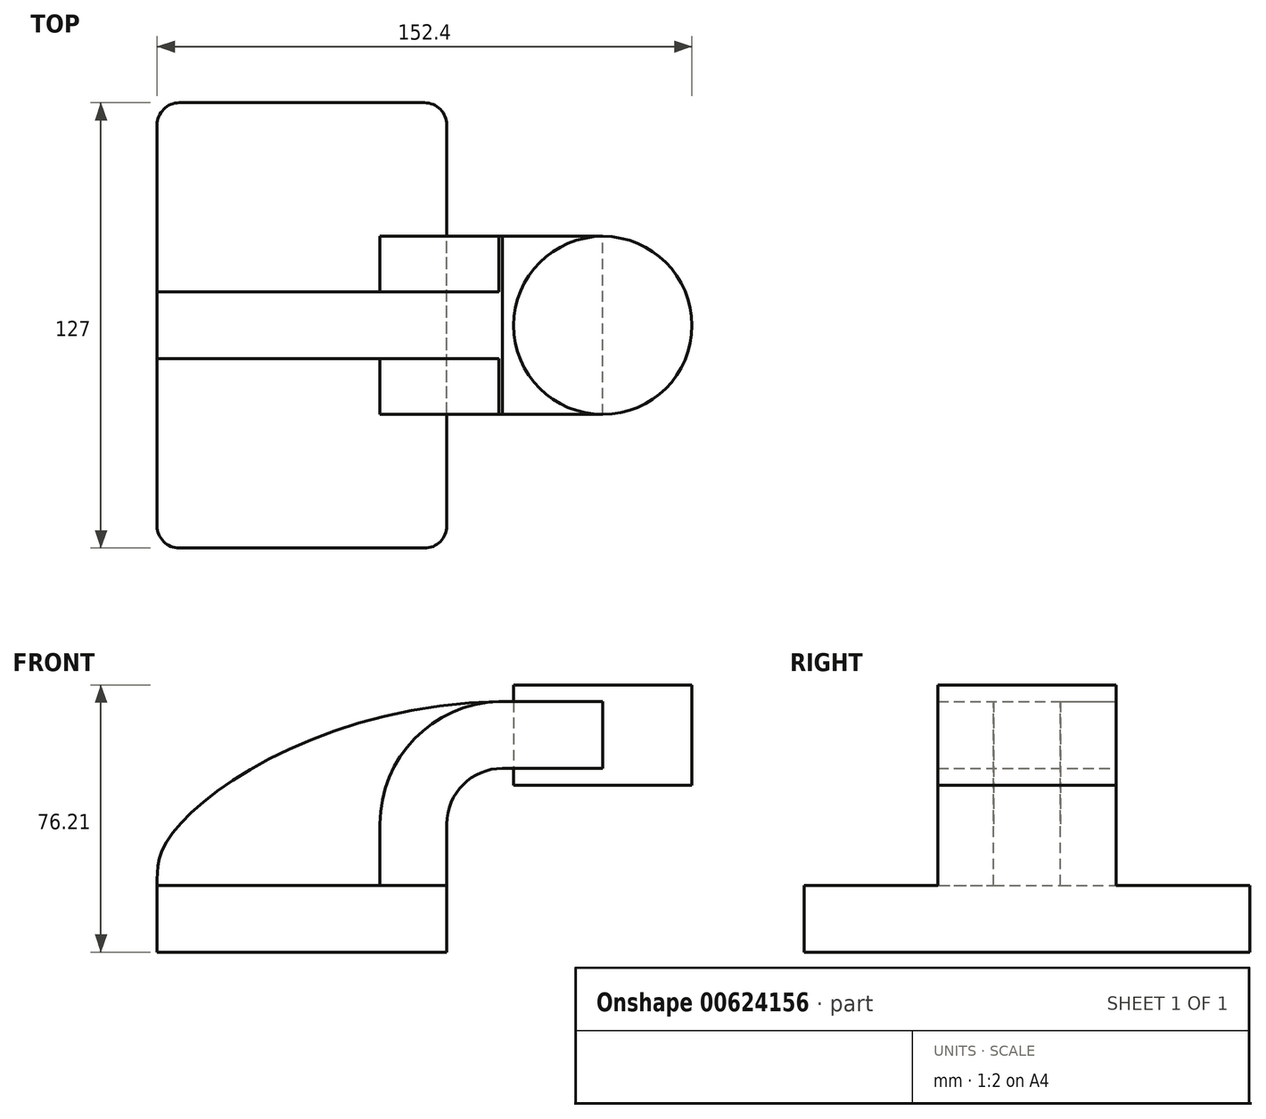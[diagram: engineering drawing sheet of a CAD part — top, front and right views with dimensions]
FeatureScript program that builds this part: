
annotation { "Feature Type Name" : "Feature", "Feature Type Description" : "" }
export const myFeature = defineFeature(function(context is Context, id is Id, definition is map)
    precondition{}
    {
        {
            var Q0;
            Q0=qCreatedBy(makeId("Front.planeOp"),FACE);
            var sketch = newSketch(context, id + "F0", { "sketchPlane" : qUnion([Q0])});
            skLineSegment(sketch, "E0.bottom", {"start": v(41.8, 9.52) * mm, "end": v(-40.75, 9.53) * mm});
            skLineSegment(sketch, "E0.top", {"start": v(41.8, -9.53) * mm, "end": v(-40.75, -9.52) * mm});
            skLineSegment(sketch, "E0.left", {"start": v(41.8, 9.52) * mm, "end": v(41.8, -9.53) * mm});
            skLineSegment(sketch, "E0.right", {"start": v(-40.75, 9.53) * mm, "end": v(-40.75, -9.52) * mm});
            skPoint(sketch, "E0.middle", {"position": v(0.53, 0) * mm});
            skLineSegment(sketch, "E1.bottom", {"start": v(60.85, 66.67) * mm, "end": v(111.65, 66.67) * mm});
            skLineSegment(sketch, "E1.top", {"start": v(60.85, 38.1) * mm, "end": v(111.65, 38.1) * mm});
            skLineSegment(sketch, "E1.left", {"start": v(60.85, 66.67) * mm, "end": v(60.85, 38.1) * mm});
            skLineSegment(sketch, "E1.right", {"start": v(111.65, 66.67) * mm, "end": v(111.65, 38.1) * mm});
            skPoint(sketch, "E1.middle", {"position": v(86.25, 52.39) * mm});
            skPoint(sketch, "E2.endSnap0", {"position": v(60.85, 52.39) * mm});
            skLineSegment(sketch, "E3", {"start": v(41.8, 9.52) * mm, "end": v(41.8, 27) * mm});
            skArc(sketch, "E4", {"start": v(41.8, 27) * mm, "mid": v(46.45, 38.23) * mm, "end": v(57.68, 42.88) * mm});
            skLineSegment(sketch, "E5", {"start": v(57.68, 42.88) * mm, "end": v(86.25, 42.88) * mm});
            skLineSegment(sketch, "E6.0", {"start": v(57.68, 61.93) * mm, "end": v(86.25, 61.93) * mm});
            skArc(sketch, "E6.1", {"start": v(22.75, 27) * mm, "mid": v(32.98, 51.7) * mm, "end": v(57.68, 61.93) * mm});
            skLineSegment(sketch, "E6.2", {"start": v(22.75, 9.52) * mm, "end": v(22.75, 27) * mm});
            skLineSegment(sketch, "E7", {"start": v(86.25, 38.1) * mm, "end": v(86.25, 66.67) * mm});
            skFitSpline(sketch, "E8", {"points": [v(-40.75, 9.52) * mm, v(-38.27, 21.6) * mm, v(57.68, 61.93) * mm], "startDerivative": vector(1.49, 38.85) * mm, "endDerivative": vector(202.41, 2.3) * mm});
            skSolve(sketch);
        }
        {
            var Q0;
            Q0=makeQuery(id+"F0.imprint","IMPRINT",FACE,{"disambiguationData":[TD([[makeQuery(id+"F0.imprint","IMPRINT",EDGE,{"derivedFrom":sQuery(id+"F0.wireOp",EDGE,"E0.top")}),-1.0]])]});
            extrude(context, id + "F1", {"entities" : qUnion([Q0]), "endBound" : BoundingType.SYMMETRIC, "depth" : 127 * mm, "offsetDistance" : 25.4 * mm});
        }
        {
            var Q0;
            {var subQ1=sQuery(id+"F0.wireOp",EDGE,"E3");Q0=makeQuery(id+"F0.imprint","IMPRINT",FACE,{"disambiguationData":[TD([[makeQuery(id+"F0.imprint","IMPRINT",EDGE,{"derivedFrom":subQ1}),1.0]])]});}
            var Q1;
            {var subQ0=sQuery(id+"F0.wireOp",EDGE,"E6.0");var subQ1=sQuery(id+"F0.wireOp",EDGE,"E1.left");var subQ2=makeQuery(id+"F0.imprint","INTERSECT",VERTEX,{"derivedFrom":[subQ1,subQ0]});Q1=makeQuery(id+"F0.imprint","IMPRINT",FACE,{"disambiguationData":[TD([[makeQuery(id+"F0.imprint","IMPRINT",EDGE,{"disambiguationData":[TD([[subQ2,-1.0]])],"derivedFrom":subQ1}),1.0]])]});}
            extrude(context, id + "F2", {"entities" : qUnion([Q0, Q1]), "operationType" : NewBodyOperationType.ADD, "endBound" : BoundingType.SYMMETRIC, "depth" : 50.8 * mm, "offsetDistance" : 25.4 * mm});
        }
        {
            var Q0;
            {var subQ3=sQuery(id+"F0.wireOp",EDGE,"E6.2");Q0=makeQuery(id+"F0.imprint","IMPRINT",FACE,{"disambiguationData":[TD([[makeQuery(id+"F0.imprint","IMPRINT",EDGE,{"derivedFrom":subQ3}),1.0]])]});}
            extrude(context, id + "F3", {"entities" : qUnion([Q0]), "operationType" : NewBodyOperationType.ADD, "endBound" : BoundingType.SYMMETRIC, "depth" : 19.05 * mm, "offsetDistance" : 25.4 * mm});
        }
        {
            var Q0;
            {var subQ4=sQuery(id+"F0.wireOp",EDGE,"E1.right");Q0=makeQuery(id+"F0.imprint","IMPRINT",FACE,{"disambiguationData":[TD([[makeQuery(id+"F0.imprint","IMPRINT",EDGE,{"derivedFrom":subQ4}),-1.0]])]});}
            var Q1;
            Q1=sQuery(id+"F0.wireOp",EDGE,"E7");
            revolve(context, id + "F4", {"entities" : qUnion([Q0]), "axis" : qUnion([Q1]), "revolveType" : RevolveType.FULL});
        }
        {
            var Q0;
            Q0=makeQuery(id+"F1.opExtrude","CAP_EDGE",EDGE,{"disambiguationData":[OSD([sQuery(id+"F0.wireOp",EDGE,"E0.right")])],"isStart":false});
            var Q1;
            Q1=makeQuery(id+"F1.opExtrude","CAP_EDGE",EDGE,{"disambiguationData":[OSD([sQuery(id+"F0.wireOp",EDGE,"E0.left")])],"isStart":false});
            var Q2;
            Q2=makeQuery(id+"F1.opExtrude","CAP_EDGE",EDGE,{"disambiguationData":[OSD([sQuery(id+"F0.wireOp",EDGE,"E0.left")])],"isStart":true});
            var Q3;
            Q3=makeQuery(id+"F1.opExtrude","CAP_EDGE",EDGE,{"disambiguationData":[OSD([sQuery(id+"F0.wireOp",EDGE,"E0.right")])],"isStart":true});
            fillet(context, id + "F5", {"entities" : qUnion([Q0, Q1, Q2, Q3]), "radius" : 6.35 * mm, "tangentPropagation" : true, "allowEdgeOverflow" : false});
        }
    });
